# Revit family: Bowl_Stools_BIM
name_source: partatom
category: Arredi
units: mm (PartAtom-declared; Revit-internal decimal feet)

## family parameters
Attiva taglio nelle viste = No
Basato su piano di lavoro = No
Condiviso = No
Numero OmniClass = 23.40.20.00
Origine composizione di rendering = Geometria famiglia
Punto di calcolo locali = No
Sempre verticale = Sì
Taglio con vuoti quando caricato = No
Titolo OmniClass = General Furniture and Specialties

## types (3) — shared parameters
AVAILABLE FINISHES = Ebonized black lacquer on Oak (EB). Raw effect lacquer on Oak (RE). Hand rubbed natural oil on Oak or Walnut (NA), or hand rubbed black oil on Walnut (BO).
BASE MATERIAL = BASSAM_FELLOWS_OAK_O-NA
BIM BADGE = https://bim.archiproducts.com
COLLECTION = Bowl
Descrizione = Solid wood stool
PRODUCT SHEET = https://www.archiproducts.com
Produttore = BassamFellows
TECHNICAL SHEET = https://bassamfellows.com
URL = https://bassamfellows.com
zero-valued in all types: Prospetto di default

## per-type parameters (varying)
| type | DIAMETER | FOOTREST | FOOTREST HIGH | FOOTREST VISIBILTY | HEIGHT | MATERIAL DESCRIPTION | Modello | RADIUS |
| CB-213 | 462 mm  [stored 1.51575 ft] | BASSAM_FELLOWS_METAL_BZ | 250 mm  [stored 0.82021 ft] | Sì | 776 mm  [stored 2.54593 ft] | Carved solid wood. Brushed stainless steel footrest | Bowl Bar Stool | 231 mm  [stored 0.757874 ft] |
| CB-212 | 449 mm  [stored 1.4731 ft] | BASSAM_FELLOWS_METAL_BZ | 150 mm | Sì | 637 mm  [stored 2.0899 ft] | Carved solid wood. Brushed stainless steel footrest | Bowl Counter Stool | 225 mm  [stored 0.738189 ft] |
| CB-211 | 462 mm  [stored 1.51575 ft] | <Per categoria> | 150 mm | No | 450 mm  [stored 1.47638 ft] | Carved solid wood | Bowl Stool/Side Table | 231 mm  [stored 0.757874 ft] |

note: column(s) folded — value = type name in every type: PRODUCT CODE

note: [stored X ft] marks values corroborated as IEEE doubles in the binary element streams (Revit-internal decimal feet)

## geometry (parser evidence)
native form markers: Sweep x1
no freeform markers — native parametric forms only
